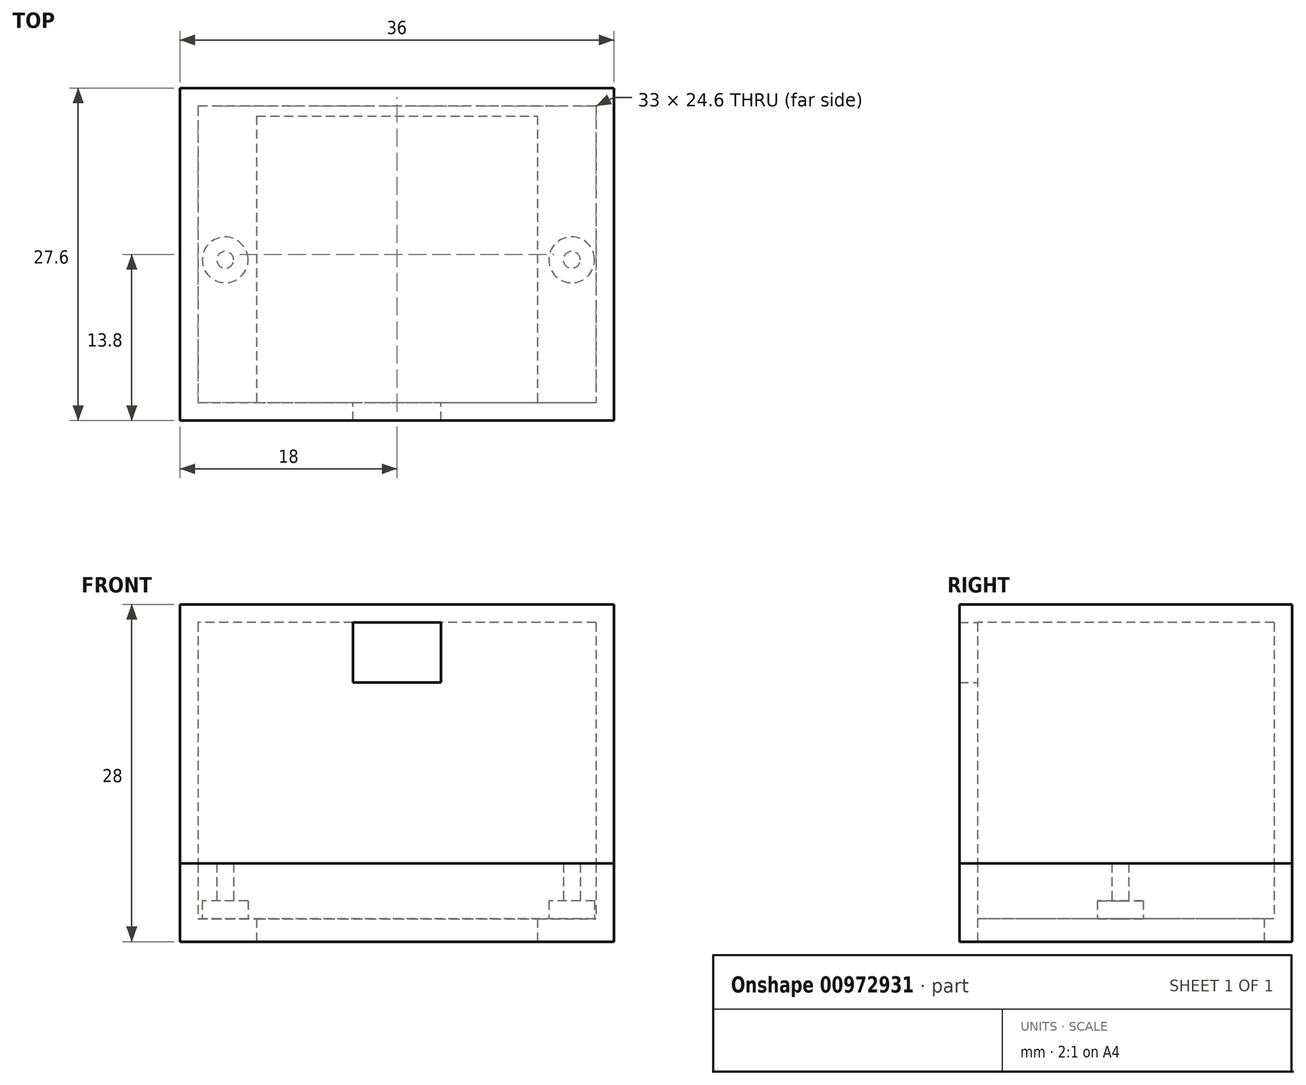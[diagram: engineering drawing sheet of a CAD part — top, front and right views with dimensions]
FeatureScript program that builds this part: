
annotation { "Feature Type Name" : "Feature", "Feature Type Description" : "" }
export const myFeature = defineFeature(function(context is Context, id is Id, definition is map)
    precondition{}
    {
        {
            var Q0;
            Q0=qCreatedBy(makeId("Top.planeOp"),FACE);
            var sketch = newSketch(context, id + "F0", { "sketchPlane" : qUnion([Q0])});
            skLineSegment(sketch, "E0.bottom", {"start": v(18, -13.8) * mm, "end": v(-18, -13.8) * mm});
            skLineSegment(sketch, "E0.top", {"start": v(18, 13.8) * mm, "end": v(-18, 13.8) * mm});
            skLineSegment(sketch, "E0.left", {"start": v(18, -13.8) * mm, "end": v(18, 13.8) * mm});
            skLineSegment(sketch, "E0.right", {"start": v(-18, -13.8) * mm, "end": v(-18, 13.8) * mm});
            skPoint(sketch, "E0.middle", {"position": v(0, 0) * mm});
            skLineSegment(sketch, "E1", {"start": v(16.5, 12.3) * mm, "end": v(-16.5, 12.3) * mm});
            skLineSegment(sketch, "E2", {"start": v(-16.5, -12.3) * mm, "end": v(16.5, -12.3) * mm});
            skLineSegment(sketch, "E3.bottom", {"start": v(-11.65, 11.5) * mm, "end": v(11.65, 11.5) * mm});
            skLineSegment(sketch, "E3.top", {"start": v(-11.65, -12.3) * mm, "end": v(11.65, -12.3) * mm});
            skLineSegment(sketch, "E3.left", {"start": v(-11.65, 11.5) * mm, "end": v(-11.65, -12.3) * mm});
            skLineSegment(sketch, "E3.right", {"start": v(11.65, 11.5) * mm, "end": v(11.65, -12.3) * mm});
            skPoint(sketch, "E4.orphan", {"position": v(18, 12.3) * mm});
            skPoint(sketch, "E5.orphan", {"position": v(18, -12.3) * mm});
            skCircle(sketch, "E6", {"center": v(14.5, -0.45) * mm, "radius": 0.7 * mm});
            skCircle(sketch, "E7", {"center": v(-14.25, -0.45) * mm, "radius": 0.7 * mm});
            skLineSegment(sketch, "E8", {"start": v(16.5, 12.3) * mm, "end": v(16.5, -12.3) * mm});
            skLineSegment(sketch, "E9", {"start": v(-16.5, 12.3) * mm, "end": v(-16.5, -12.3) * mm});
            skCircle(sketch, "E10.0", {"center": v(-14.25, -0.45) * mm, "radius": 1.9 * mm});
            skCircle(sketch, "E11.0", {"center": v(14.5, -0.45) * mm, "radius": 1.9 * mm});
            skSolve(sketch);
        }
        {
            var Q0;
            Q0=makeQuery(id+"F0.imprint","IMPRINT",FACE,{"disambiguationData":[TD([[makeQuery(id+"F0.imprint","IMPRINT",EDGE,{"derivedFrom":sQuery(id+"F0.wireOp",EDGE,"E1")}),1.0]])]});
            extrude(context, id + "F1", {"entities" : qUnion([Q0]), "depth" : 1.9 * mm, "offsetDistance" : 25 * mm});
        }
        {
            var Q0;
            Q0 = qSketchRegion(id + "F0", true);
            extrude(context, id + "F2", {"entities" : qUnion([Q0]), "operationType" : NewBodyOperationType.ADD, "depth" : 6.5 * mm, "offsetDistance" : 25 * mm});
        }
        {
            var Q0;
            Q0=makeQuery(id+"F0.imprint","IMPRINT",FACE,{"disambiguationData":[TD([[makeQuery(id+"F0.imprint","IMPRINT",EDGE,{"derivedFrom":sQuery(id+"F0.wireOp",EDGE,"E7")}),-1.0]])]});
            var Q1;
            Q1=makeQuery(id+"F0.imprint","IMPRINT",FACE,{"disambiguationData":[TD([[makeQuery(id+"F0.imprint","IMPRINT",EDGE,{"derivedFrom":sQuery(id+"F0.wireOp",EDGE,"E6")}),-1.0]])]});
            extrude(context, id + "F3", {"entities" : qUnion([Q0, Q1]), "operationType" : NewBodyOperationType.ADD, "depth" : 3.4 * mm, "offsetDistance" : 25 * mm});
        }
        {
            var Q0;
            Q0=makeQuery(id+"F0.imprint","IMPRINT",FACE,{"disambiguationData":[TD([[makeQuery(id+"F0.imprint","IMPRINT",EDGE,{"derivedFrom":sQuery(id+"F0.wireOp",EDGE,"E7")}),1.0]])]});
            var Q1;
            Q1=makeQuery(id+"F0.imprint","IMPRINT",FACE,{"disambiguationData":[TD([[makeQuery(id+"F0.imprint","IMPRINT",EDGE,{"derivedFrom":sQuery(id+"F0.wireOp",EDGE,"E6")}),1.0]])]});
            extrude(context, id + "F4", {"entities" : qUnion([Q0, Q1]), "operationType" : NewBodyOperationType.ADD, "depth" : 6.5 * mm, "offsetDistance" : 25 * mm});
        }
        {
            var Q0;
            Q0=makeQuery(id+"F2.opExtrude","CAP_FACE",FACE,{"disambiguationData":[OSD([sQuery(id+"F0.wireOp",EDGE,"E0.bottom"),sQuery(id+"F0.wireOp",EDGE,"E0.top"),sQuery(id+"F0.wireOp",EDGE,"E0.left"),sQuery(id+"F0.wireOp",EDGE,"E0.right"),sQuery(id+"F0.wireOp",EDGE,"E1"),sQuery(id+"F0.wireOp",EDGE,"E2"),sQuery(id+"F0.wireOp",EDGE,"E3.top"),sQuery(id+"F0.wireOp",EDGE,"E8"),sQuery(id+"F0.wireOp",EDGE,"E9")])],"isStart":false});
            var sketch = newSketch(context, id + "F5", { "sketchPlane" : qUnion([Q0])});
            skLineSegment(sketch, "E12.bottom", {"start": v(-18, 13.8) * mm, "end": v(18, 13.8) * mm});
            skLineSegment(sketch, "E12.top", {"start": v(-18, -13.8) * mm, "end": v(18, -13.8) * mm});
            skLineSegment(sketch, "E12.left", {"start": v(-18, 13.8) * mm, "end": v(-18, -13.8) * mm});
            skLineSegment(sketch, "E12.right", {"start": v(18, 13.8) * mm, "end": v(18, -13.8) * mm});
            skLineSegment(sketch, "E13.bottom", {"start": v(-16.5, 12.3) * mm, "end": v(16.5, 12.3) * mm});
            skLineSegment(sketch, "E13.top", {"start": v(-16.5, -12.3) * mm, "end": v(16.5, -12.3) * mm});
            skLineSegment(sketch, "E13.left", {"start": v(-16.5, 12.3) * mm, "end": v(-16.5, -12.3) * mm});
            skLineSegment(sketch, "E13.right", {"start": v(16.5, 12.3) * mm, "end": v(16.5, -12.3) * mm});
            skSolve(sketch);
        }
        {
            var Q0;
            Q0 = qSketchRegion(id + "F5", true);
            extrude(context, id + "F6", {"entities" : qUnion([Q0]), "depth" : 15 * mm, "offsetDistance" : 25 * mm});
        }
        {
            var Q0;
            Q0=makeQuery(id+"F6.opExtrude","CAP_FACE",FACE,{"disambiguationData":[OSD([sQuery(id+"F5.wireOp",EDGE,"E12.bottom"),sQuery(id+"F5.wireOp",EDGE,"E12.top"),sQuery(id+"F5.wireOp",EDGE,"E12.left"),sQuery(id+"F5.wireOp",EDGE,"E12.right"),sQuery(id+"F5.wireOp",EDGE,"E13.bottom"),sQuery(id+"F5.wireOp",EDGE,"E13.top"),sQuery(id+"F5.wireOp",EDGE,"E13.left"),sQuery(id+"F5.wireOp",EDGE,"E13.right")])],"isStart":false});
            var sketch = newSketch(context, id + "F7", { "sketchPlane" : qUnion([Q0])});
            skLineSegment(sketch, "E14", {"start": v(-16.5, 12.3) * mm, "end": v(-16.5, -12.3) * mm});
            skLineSegment(sketch, "E15", {"start": v(16.5, -12.3) * mm, "end": v(16.5, 12.3) * mm});
            skLineSegment(sketch, "E16", {"start": v(-18, 13.8) * mm, "end": v(-18, -13.8) * mm});
            skLineSegment(sketch, "E17", {"start": v(18, -13.8) * mm, "end": v(18, 13.8) * mm});
            skLineSegment(sketch, "E18", {"start": v(18, -13.8) * mm, "end": v(3.65, -13.8) * mm});
            skLineSegment(sketch, "E19", {"start": v(-18, -13.8) * mm, "end": v(-3.65, -13.8) * mm});
            skLineSegment(sketch, "E20", {"start": v(-3.65, -13.8) * mm, "end": v(-3.65, -12.3) * mm});
            skLineSegment(sketch, "E21", {"start": v(-3.65, -12.3) * mm, "end": v(-16.5, -12.3) * mm});
            skLineSegment(sketch, "E22", {"start": v(3.65, -13.8) * mm, "end": v(3.65, -12.3) * mm});
            skLineSegment(sketch, "E23", {"start": v(3.65, -12.3) * mm, "end": v(16.5, -12.3) * mm});
            skLineSegment(sketch, "E24", {"start": v(-18, 13.8) * mm, "end": v(18, 13.8) * mm});
            skLineSegment(sketch, "E25", {"start": v(16.5, 12.3) * mm, "end": v(-16.5, 12.3) * mm});
            skSolve(sketch);
        }
        {
            var Q0;
            Q0=makeQuery(id+"F7.imprint","IMPRINT",FACE,{"disambiguationData":[TD([[makeQuery(id+"F7.imprint","IMPRINT",EDGE,{"derivedFrom":sQuery(id+"F7.wireOp",EDGE,"E14")}),-1.0]])]});
            extrude(context, id + "F8", {"entities" : qUnion([Q0]), "operationType" : NewBodyOperationType.ADD, "depth" : 5 * mm, "offsetDistance" : 25 * mm});
        }
        {
            var Q0;
            Q0=makeQuery(id+"F8.opExtrude","CAP_FACE",FACE,{"disambiguationData":[OSD([sQuery(id+"F7.wireOp",EDGE,"rRFBu7w7-P3lb-jCwk-6rKF-AQtsvLB6tisc"),sQuery(id+"F7.wireOp",EDGE,"ppwkOFOh-RFGn-ke6n-XWSh-DkzSVNa4xqwI"),sQuery(id+"F7.wireOp",EDGE,"klr6Fp9D-riRU-nvDd-WRFo-yGBtE52DJbJj"),sQuery(id+"F7.wireOp",EDGE,"E14"),sQuery(id+"F7.wireOp",EDGE,"2UbSxQzu-qqSD-NMRT-4Rfq-7Zizc25jd9m2"),sQuery(id+"F7.wireOp",EDGE,"E15"),sQuery(id+"F7.wireOp",EDGE,"E16"),sQuery(id+"F7.wireOp",EDGE,"iXUShxzM-zD4U-kIIV-bdlI-gwJT2ngj7i7Q"),sQuery(id+"F7.wireOp",EDGE,"E17"),sQuery(id+"F7.wireOp",EDGE,"bWlHCirX-Aw2E-GPpJ-ZWm7-9ac9hPzvujZ5"),sQuery(id+"F7.wireOp",EDGE,"yd4FpnGY-Netx-T1EG-vry9-zwEfc6c2tXIC"),sQuery(id+"F7.wireOp",EDGE,"AN3h4VbA-NttB-XurW-1vM4-Ce7KdtP1WdbR")])],"isStart":false});
            var sketch = newSketch(context, id + "F9", { "sketchPlane" : qUnion([Q0])});
            skLineSegment(sketch, "E26.bottom", {"start": v(-18, 13.8) * mm, "end": v(18, 13.8) * mm});
            skLineSegment(sketch, "E26.top", {"start": v(-18, -13.8) * mm, "end": v(18, -13.8) * mm});
            skLineSegment(sketch, "E26.left", {"start": v(-18, 13.8) * mm, "end": v(-18, -13.8) * mm});
            skLineSegment(sketch, "E26.right", {"start": v(18, 13.8) * mm, "end": v(18, -13.8) * mm});
            skSolve(sketch);
        }
        {
            var Q0;
            Q0 = qSketchRegion(id + "F9", true);
            extrude(context, id + "F10", {"entities" : qUnion([Q0]), "operationType" : NewBodyOperationType.ADD, "depth" : 1.5 * mm, "offsetDistance" : 25 * mm});
        }
    });
